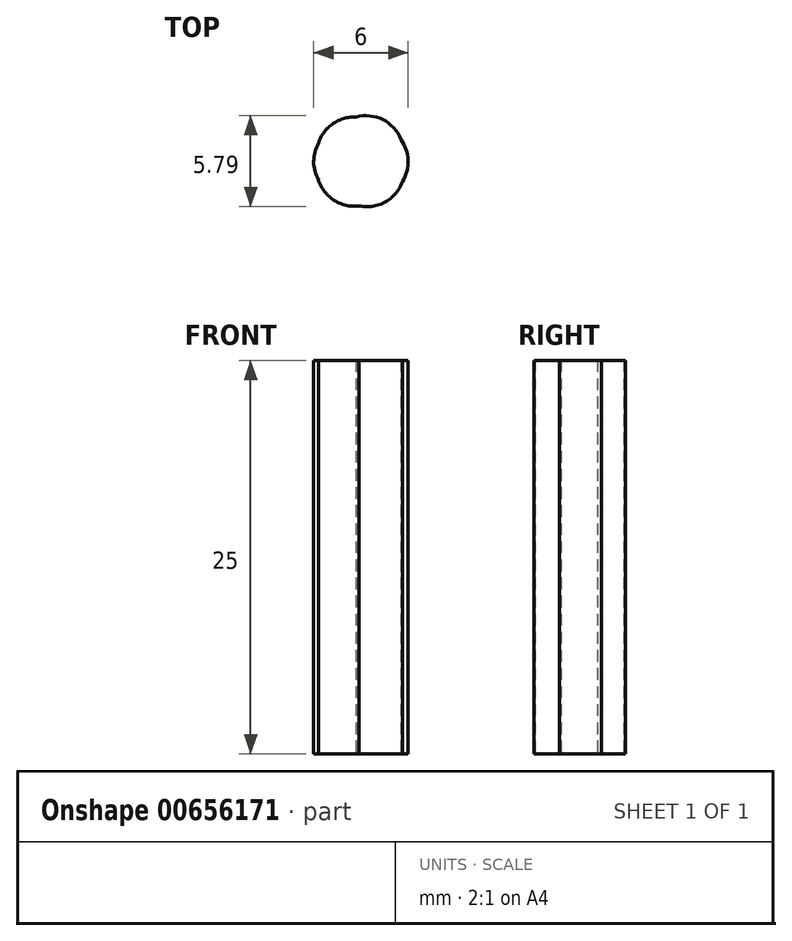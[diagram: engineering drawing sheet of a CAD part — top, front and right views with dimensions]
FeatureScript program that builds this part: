
annotation { "Feature Type Name" : "Feature", "Feature Type Description" : "" }
export const myFeature = defineFeature(function(context is Context, id is Id, definition is map)
    precondition{}
    {
        {
            var Q0;
            Q0=qCreatedBy(makeId("Top.planeOp"),FACE);
            var sketch = newSketch(context, id + "F0", { "sketchPlane" : qUnion([Q0])});
            skCircle(sketch, "E0", {"center": v(0, 0) * mm, "radius": 3 * mm});
            skCircle(sketch, "E1", {"center": v(0.6, 0) * mm, "radius": 2.4 * mm});
            skCircle(sketch, "E2", {"center": v(-0.6, 0) * mm, "radius": 2.4 * mm});
            skCircle(sketch, "E3", {"center": v(-0.41, -0.43) * mm, "radius": 2.4 * mm});
            skCircle(sketch, "E4", {"center": v(0.38, -0.47) * mm, "radius": 2.4 * mm});
            skCircle(sketch, "E5", {"center": v(-0.41, 0.44) * mm, "radius": 2.4 * mm});
            skCircle(sketch, "E6", {"center": v(0.32, 0.52) * mm, "radius": 2.4 * mm});
            skSolve(sketch);
        }
        {
            var Q0;
            {var subQ0=sQuery(id+"F0.wireOp",EDGE,"E6");var subQ1=sQuery(id+"F0.wireOp",EDGE,"E0");var subQ2=makeQuery(id+"F0.imprint","INTERSECT",VERTEX,{"disambiguationData":[OD(0.0)],"derivedFrom":[subQ1,subQ0]});Q0=makeQuery(id+"F0.imprint","IMPRINT",FACE,{"disambiguationData":[TD([[makeQuery(id+"F0.imprint","IMPRINT",EDGE,{"disambiguationData":[TD([[subQ2,-1.0]])],"derivedFrom":subQ1}),-1.0]])]});}
            var Q1;
            {var subQ0=sQuery(id+"F0.wireOp",EDGE,"E2");var subQ1=makeQuery(id+"F0.imprint","INTERSECT",VERTEX,{"derivedFrom":[sQuery(id+"F0.wireOp",EDGE,"E0"),subQ0]});Q1=makeQuery(id+"F0.imprint","IMPRINT",FACE,{"disambiguationData":[TD([[makeQuery(id+"F0.imprint","IMPRINT",EDGE,{"disambiguationData":[TD([[subQ1,1.0]])],"derivedFrom":subQ0}),1.0]])]});}
            var Q2;
            {var subQ0=sQuery(id+"F0.wireOp",EDGE,"E5");var subQ1=sQuery(id+"F0.wireOp",EDGE,"E1");var subQ2=makeQuery(id+"F0.imprint","INTERSECT",VERTEX,{"disambiguationData":[OD(0.0)],"derivedFrom":[subQ1,subQ0]});Q2=makeQuery(id+"F0.imprint","IMPRINT",FACE,{"disambiguationData":[TD([[makeQuery(id+"F0.imprint","IMPRINT",EDGE,{"disambiguationData":[TD([[subQ2,-1.0]])],"derivedFrom":subQ1}),-1.0]])]});}
            var Q3;
            {var subQ3=sQuery(id+"F0.wireOp",EDGE,"E2");var subQ5=sQuery(id+"F0.wireOp",EDGE,"E6");var subQ6=makeQuery(id+"F0.imprint","INTERSECT",VERTEX,{"disambiguationData":[OD(0.0)],"derivedFrom":[subQ3,subQ5]});Q3=makeQuery(id+"F0.imprint","IMPRINT",FACE,{"disambiguationData":[TD([[makeQuery(id+"F0.imprint","IMPRINT",EDGE,{"disambiguationData":[TD([[subQ6,-1.0]])],"derivedFrom":subQ3}),-1.0]])]});}
            var Q4;
            {var subQ0=sQuery(id+"F0.wireOp",EDGE,"E6");var subQ1=sQuery(id+"F0.wireOp",EDGE,"E3");var subQ2=makeQuery(id+"F0.imprint","INTERSECT",VERTEX,{"disambiguationData":[OD(0.0)],"derivedFrom":[subQ1,subQ0]});Q4=makeQuery(id+"F0.imprint","IMPRINT",FACE,{"disambiguationData":[TD([[makeQuery(id+"F0.imprint","IMPRINT",EDGE,{"disambiguationData":[TD([[subQ2,-1.0]])],"derivedFrom":subQ1}),1.0]])]});}
            var Q5;
            {var subQ0=sQuery(id+"F0.wireOp",EDGE,"E6");var subQ1=sQuery(id+"F0.wireOp",EDGE,"E2");var subQ2=makeQuery(id+"F0.imprint","INTERSECT",VERTEX,{"disambiguationData":[OD(0.0)],"derivedFrom":[subQ1,subQ0]});Q5=makeQuery(id+"F0.imprint","IMPRINT",FACE,{"disambiguationData":[TD([[makeQuery(id+"F0.imprint","IMPRINT",EDGE,{"disambiguationData":[TD([[subQ2,-1.0]])],"derivedFrom":subQ1}),1.0]])]});}
            var Q6;
            {var subQ0=sQuery(id+"F0.wireOp",EDGE,"E3");var subQ1=sQuery(id+"F0.wireOp",EDGE,"E1");var subQ2=makeQuery(id+"F0.imprint","INTERSECT",VERTEX,{"disambiguationData":[OD(0.0)],"derivedFrom":[subQ1,subQ0]});Q6=makeQuery(id+"F0.imprint","IMPRINT",FACE,{"disambiguationData":[TD([[makeQuery(id+"F0.imprint","IMPRINT",EDGE,{"disambiguationData":[TD([[subQ2,-1.0]])],"derivedFrom":subQ1}),-1.0]])]});}
            var Q7;
            {var subQ0=sQuery(id+"F0.wireOp",EDGE,"E2");var subQ1=sQuery(id+"F0.wireOp",EDGE,"E1");var subQ2=makeQuery(id+"F0.imprint","INTERSECT",VERTEX,{"disambiguationData":[OD(0.0)],"derivedFrom":[subQ1,subQ0]});Q7=makeQuery(id+"F0.imprint","IMPRINT",FACE,{"disambiguationData":[TD([[makeQuery(id+"F0.imprint","IMPRINT",EDGE,{"disambiguationData":[TD([[subQ2,-1.0]])],"derivedFrom":subQ1}),-1.0]])]});}
            var Q8;
            {var subQ0=sQuery(id+"F0.wireOp",EDGE,"E2");var subQ1=sQuery(id+"F0.wireOp",EDGE,"E1");var subQ2=makeQuery(id+"F0.imprint","INTERSECT",VERTEX,{"disambiguationData":[OD(0.0)],"derivedFrom":[subQ1,subQ0]});Q8=makeQuery(id+"F0.imprint","IMPRINT",FACE,{"disambiguationData":[TD([[makeQuery(id+"F0.imprint","IMPRINT",EDGE,{"disambiguationData":[TD([[subQ2,-1.0]])],"derivedFrom":subQ1}),1.0]])]});}
            var Q9;
            {var subQ0=sQuery(id+"F0.wireOp",EDGE,"E5");var subQ1=sQuery(id+"F0.wireOp",EDGE,"E1");var subQ2=makeQuery(id+"F0.imprint","INTERSECT",VERTEX,{"disambiguationData":[OD(0.0)],"derivedFrom":[subQ1,subQ0]});Q9=makeQuery(id+"F0.imprint","IMPRINT",FACE,{"disambiguationData":[TD([[makeQuery(id+"F0.imprint","IMPRINT",EDGE,{"disambiguationData":[TD([[subQ2,-1.0]])],"derivedFrom":subQ1}),1.0]])]});}
            var Q10;
            {var subQ0=sQuery(id+"F0.wireOp",EDGE,"E6");var subQ1=sQuery(id+"F0.wireOp",EDGE,"E0");var subQ2=makeQuery(id+"F0.imprint","INTERSECT",VERTEX,{"disambiguationData":[OD(0.0)],"derivedFrom":[subQ1,subQ0]});Q10=makeQuery(id+"F0.imprint","IMPRINT",FACE,{"disambiguationData":[TD([[makeQuery(id+"F0.imprint","IMPRINT",EDGE,{"disambiguationData":[TD([[subQ2,-1.0]])],"derivedFrom":subQ1}),1.0]])]});}
            var Q11;
            {var subQ0=sQuery(id+"F0.wireOp",EDGE,"E6");var subQ1=sQuery(id+"F0.wireOp",EDGE,"E1");var subQ2=makeQuery(id+"F0.imprint","INTERSECT",VERTEX,{"disambiguationData":[OD(0.0)],"derivedFrom":[subQ1,subQ0]});Q11=makeQuery(id+"F0.imprint","IMPRINT",FACE,{"disambiguationData":[TD([[makeQuery(id+"F0.imprint","IMPRINT",EDGE,{"disambiguationData":[TD([[subQ2,-1.0]])],"derivedFrom":subQ1}),1.0]])]});}
            var Q12;
            {var subQ0=sQuery(id+"F0.wireOp",EDGE,"E1");var subQ1=makeQuery(id+"F0.imprint","INTERSECT",VERTEX,{"derivedFrom":[sQuery(id+"F0.wireOp",EDGE,"E0"),subQ0]});Q12=makeQuery(id+"F0.imprint","IMPRINT",FACE,{"disambiguationData":[TD([[makeQuery(id+"F0.imprint","IMPRINT",EDGE,{"disambiguationData":[TD([[subQ1,-1.0]])],"derivedFrom":subQ0}),1.0]])]});}
            var Q13;
            {var subQ4=sQuery(id+"F0.wireOp",EDGE,"E3");var subQ6=sQuery(id+"F0.wireOp",EDGE,"E1");var subQ7=makeQuery(id+"F0.imprint","INTERSECT",VERTEX,{"disambiguationData":[OD(1.0)],"derivedFrom":[subQ6,subQ4]});Q13=makeQuery(id+"F0.imprint","IMPRINT",FACE,{"disambiguationData":[TD([[makeQuery(id+"F0.imprint","IMPRINT",EDGE,{"disambiguationData":[TD([[subQ7,-1.0]])],"derivedFrom":subQ6}),-1.0]])]});}
            var Q14;
            {var subQ0=sQuery(id+"F0.wireOp",EDGE,"E3");var subQ5=sQuery(id+"F0.wireOp",EDGE,"E2");var subQ8=makeQuery(id+"F0.imprint","INTERSECT",VERTEX,{"disambiguationData":[OD(1.0)],"derivedFrom":[subQ5,subQ0]});Q14=makeQuery(id+"F0.imprint","IMPRINT",FACE,{"disambiguationData":[TD([[makeQuery(id+"F0.imprint","IMPRINT",EDGE,{"disambiguationData":[TD([[subQ8,-1.0]])],"derivedFrom":subQ5}),-1.0]])]});}
            var Q15;
            {var subQ0=sQuery(id+"F0.wireOp",EDGE,"E3");var subQ1=sQuery(id+"F0.wireOp",EDGE,"E2");var subQ2=makeQuery(id+"F0.imprint","INTERSECT",VERTEX,{"disambiguationData":[OD(1.0)],"derivedFrom":[subQ1,subQ0]});Q15=makeQuery(id+"F0.imprint","IMPRINT",FACE,{"disambiguationData":[TD([[makeQuery(id+"F0.imprint","IMPRINT",EDGE,{"disambiguationData":[TD([[subQ2,-1.0]])],"derivedFrom":subQ1}),1.0]])]});}
            var Q16;
            {var subQ0=sQuery(id+"F0.wireOp",EDGE,"E5");var subQ1=sQuery(id+"F0.wireOp",EDGE,"E1");var subQ2=makeQuery(id+"F0.imprint","INTERSECT",VERTEX,{"disambiguationData":[OD(1.0)],"derivedFrom":[subQ1,subQ0]});Q16=makeQuery(id+"F0.imprint","IMPRINT",FACE,{"disambiguationData":[TD([[makeQuery(id+"F0.imprint","IMPRINT",EDGE,{"disambiguationData":[TD([[subQ2,-1.0]])],"derivedFrom":subQ1}),-1.0]])]});}
            var Q17;
            {var subQ0=sQuery(id+"F0.wireOp",EDGE,"E6");var subQ1=sQuery(id+"F0.wireOp",EDGE,"E1");var subQ2=makeQuery(id+"F0.imprint","INTERSECT",VERTEX,{"disambiguationData":[OD(1.0)],"derivedFrom":[subQ1,subQ0]});Q17=makeQuery(id+"F0.imprint","IMPRINT",FACE,{"disambiguationData":[TD([[makeQuery(id+"F0.imprint","IMPRINT",EDGE,{"disambiguationData":[TD([[subQ2,-1.0]])],"derivedFrom":subQ1}),-1.0]])]});}
            var Q18;
            {var subQ0=sQuery(id+"F0.wireOp",EDGE,"E4");var subQ1=sQuery(id+"F0.wireOp",EDGE,"E1");var subQ2=makeQuery(id+"F0.imprint","INTERSECT",VERTEX,{"disambiguationData":[OD(0.0)],"derivedFrom":[subQ1,subQ0]});Q18=makeQuery(id+"F0.imprint","IMPRINT",FACE,{"disambiguationData":[TD([[makeQuery(id+"F0.imprint","IMPRINT",EDGE,{"disambiguationData":[TD([[subQ2,-1.0]])],"derivedFrom":subQ1}),1.0]])]});}
            var Q19;
            {var subQ0=sQuery(id+"F0.wireOp",EDGE,"E3");var subQ1=sQuery(id+"F0.wireOp",EDGE,"E1");var subQ2=makeQuery(id+"F0.imprint","INTERSECT",VERTEX,{"disambiguationData":[OD(0.0)],"derivedFrom":[subQ1,subQ0]});Q19=makeQuery(id+"F0.imprint","IMPRINT",FACE,{"disambiguationData":[TD([[makeQuery(id+"F0.imprint","IMPRINT",EDGE,{"disambiguationData":[TD([[subQ2,-1.0]])],"derivedFrom":subQ1}),1.0]])]});}
            var Q20;
            {var subQ0=sQuery(id+"F0.wireOp",EDGE,"E4");var subQ1=sQuery(id+"F0.wireOp",EDGE,"E2");var subQ2=makeQuery(id+"F0.imprint","INTERSECT",VERTEX,{"disambiguationData":[OD(0.0)],"derivedFrom":[subQ1,subQ0]});Q20=makeQuery(id+"F0.imprint","IMPRINT",FACE,{"disambiguationData":[TD([[makeQuery(id+"F0.imprint","IMPRINT",EDGE,{"disambiguationData":[TD([[subQ2,1.0]])],"derivedFrom":subQ1}),-1.0]])]});}
            var Q21;
            {var subQ0=sQuery(id+"F0.wireOp",EDGE,"E5");var subQ1=sQuery(id+"F0.wireOp",EDGE,"E3");var subQ2=makeQuery(id+"F0.imprint","INTERSECT",VERTEX,{"disambiguationData":[OD(0.0)],"derivedFrom":[subQ1,subQ0]});Q21=makeQuery(id+"F0.imprint","IMPRINT",FACE,{"disambiguationData":[TD([[makeQuery(id+"F0.imprint","IMPRINT",EDGE,{"disambiguationData":[TD([[subQ2,1.0]])],"derivedFrom":subQ1}),-1.0]])]});}
            var Q22;
            {var subQ0=sQuery(id+"F0.wireOp",EDGE,"E3");var subQ1=sQuery(id+"F0.wireOp",EDGE,"E1");var subQ2=makeQuery(id+"F0.imprint","INTERSECT",VERTEX,{"disambiguationData":[OD(1.0)],"derivedFrom":[subQ1,subQ0]});Q22=makeQuery(id+"F0.imprint","IMPRINT",FACE,{"disambiguationData":[TD([[makeQuery(id+"F0.imprint","IMPRINT",EDGE,{"disambiguationData":[TD([[subQ2,-1.0]])],"derivedFrom":subQ1}),1.0]])]});}
            var Q23;
            {var subQ0=sQuery(id+"F0.wireOp",EDGE,"E6");var subQ1=sQuery(id+"F0.wireOp",EDGE,"E2");var subQ2=makeQuery(id+"F0.imprint","INTERSECT",VERTEX,{"disambiguationData":[OD(1.0)],"derivedFrom":[subQ1,subQ0]});Q23=makeQuery(id+"F0.imprint","IMPRINT",FACE,{"disambiguationData":[TD([[makeQuery(id+"F0.imprint","IMPRINT",EDGE,{"disambiguationData":[TD([[subQ2,-1.0]])],"derivedFrom":subQ1}),1.0]])]});}
            var Q24;
            {var subQ0=sQuery(id+"F0.wireOp",EDGE,"E2");var subQ1=sQuery(id+"F0.wireOp",EDGE,"E1");var subQ2=makeQuery(id+"F0.imprint","INTERSECT",VERTEX,{"disambiguationData":[OD(1.0)],"derivedFrom":[subQ1,subQ0]});Q24=makeQuery(id+"F0.imprint","IMPRINT",FACE,{"disambiguationData":[TD([[makeQuery(id+"F0.imprint","IMPRINT",EDGE,{"disambiguationData":[TD([[subQ2,-1.0]])],"derivedFrom":subQ1}),-1.0]])]});}
            var Q25;
            {var subQ0=sQuery(id+"F0.wireOp",EDGE,"E2");var subQ1=sQuery(id+"F0.wireOp",EDGE,"E1");var subQ2=makeQuery(id+"F0.imprint","INTERSECT",VERTEX,{"disambiguationData":[OD(1.0)],"derivedFrom":[subQ1,subQ0]});Q25=makeQuery(id+"F0.imprint","IMPRINT",FACE,{"disambiguationData":[TD([[makeQuery(id+"F0.imprint","IMPRINT",EDGE,{"disambiguationData":[TD([[subQ2,-1.0]])],"derivedFrom":subQ1}),1.0]])]});}
            var Q26;
            {var subQ0=sQuery(id+"F0.wireOp",EDGE,"E5");var subQ1=sQuery(id+"F0.wireOp",EDGE,"E1");var subQ2=makeQuery(id+"F0.imprint","INTERSECT",VERTEX,{"disambiguationData":[OD(1.0)],"derivedFrom":[subQ1,subQ0]});Q26=makeQuery(id+"F0.imprint","IMPRINT",FACE,{"disambiguationData":[TD([[makeQuery(id+"F0.imprint","IMPRINT",EDGE,{"disambiguationData":[TD([[subQ2,-1.0]])],"derivedFrom":subQ1}),1.0]])]});}
            var Q27;
            {var subQ0=sQuery(id+"F0.wireOp",EDGE,"E6");var subQ1=sQuery(id+"F0.wireOp",EDGE,"E1");var subQ2=makeQuery(id+"F0.imprint","INTERSECT",VERTEX,{"disambiguationData":[OD(1.0)],"derivedFrom":[subQ1,subQ0]});Q27=makeQuery(id+"F0.imprint","IMPRINT",FACE,{"disambiguationData":[TD([[makeQuery(id+"F0.imprint","IMPRINT",EDGE,{"disambiguationData":[TD([[subQ2,-1.0]])],"derivedFrom":subQ1}),1.0]])]});}
            var Q28;
            {var subQ0=sQuery(id+"F0.wireOp",EDGE,"E4");var subQ1=sQuery(id+"F0.wireOp",EDGE,"E1");var subQ2=makeQuery(id+"F0.imprint","INTERSECT",VERTEX,{"disambiguationData":[OD(0.0)],"derivedFrom":[subQ1,subQ0]});Q28=makeQuery(id+"F0.imprint","IMPRINT",FACE,{"disambiguationData":[TD([[makeQuery(id+"F0.imprint","IMPRINT",EDGE,{"disambiguationData":[TD([[subQ2,-1.0]])],"derivedFrom":subQ1}),-1.0]])]});}
            var Q29;
            {var subQ0=sQuery(id+"F0.wireOp",EDGE,"E6");var subQ1=sQuery(id+"F0.wireOp",EDGE,"E2");var subQ2=makeQuery(id+"F0.imprint","INTERSECT",VERTEX,{"disambiguationData":[OD(1.0)],"derivedFrom":[subQ1,subQ0]});Q29=makeQuery(id+"F0.imprint","IMPRINT",FACE,{"disambiguationData":[TD([[makeQuery(id+"F0.imprint","IMPRINT",EDGE,{"disambiguationData":[TD([[subQ2,-1.0]])],"derivedFrom":subQ1}),-1.0]])]});}
            var Q30;
            {var subQ0=sQuery(id+"F0.wireOp",EDGE,"E3");var subQ1=sQuery(id+"F0.wireOp",EDGE,"E2");var subQ2=makeQuery(id+"F0.imprint","INTERSECT",VERTEX,{"disambiguationData":[OD(0.0)],"derivedFrom":[subQ1,subQ0]});Q30=makeQuery(id+"F0.imprint","IMPRINT",FACE,{"disambiguationData":[TD([[makeQuery(id+"F0.imprint","IMPRINT",EDGE,{"disambiguationData":[TD([[subQ2,1.0]])],"derivedFrom":subQ1}),-1.0]])]});}
            var Q31;
            {var subQ0=sQuery(id+"F0.wireOp",EDGE,"E4");var subQ1=sQuery(id+"F0.wireOp",EDGE,"E2");var subQ2=makeQuery(id+"F0.imprint","INTERSECT",VERTEX,{"disambiguationData":[OD(0.0)],"derivedFrom":[subQ1,subQ0]});Q31=makeQuery(id+"F0.imprint","IMPRINT",FACE,{"disambiguationData":[TD([[makeQuery(id+"F0.imprint","IMPRINT",EDGE,{"disambiguationData":[TD([[subQ2,1.0]])],"derivedFrom":subQ1}),1.0]])]});}
            extrude(context, id + "F1", {"entities" : qUnion([Q0, Q1, Q2, Q3, Q4, Q5, Q6, Q7, Q8, Q9, Q10, Q11, Q12, Q13, Q14, Q15, Q16, Q17, Q18, Q19, Q20, Q21, Q22, Q23, Q24, Q25, Q26, Q27, Q28, Q29, Q30, Q31]), "depth" : 25 * mm, "offsetDistance" : 25 * mm});
        }
    });
